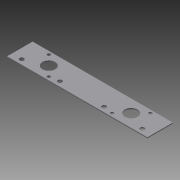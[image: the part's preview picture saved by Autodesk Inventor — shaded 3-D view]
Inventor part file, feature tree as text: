
AUTODESK INVENTOR PART (.ipt)
format: ipt  version: 2013 (Build 170138000, 138)  size: 105,472 bytes
history: native  units: in
note: dims shown in document units (in); Inventor stores cm internally (conversion verified against a paired STEP export)
features: extrude x1, sketch x1
ambient origin geometry x8: Origin, YZ Plane, XZ Plane, XY Plane, X Axis, Y Axis, Z Axis, Center Point
bodies: Solid1 (feature_tree)
feature tree (2):
  extrude  "Extrusion1"  Depth=2.75in
  sketch  "Sketch1"  dims[d0=5.5in d2=2.75in d3=1.0in d4=0.5in d5=0.125in d6=0.125in d7=4.23in d8=0.635in d9=0.125in d10=0.125in d11=1.0in d12=1.0in d13=0.125in d14=0.125in d15=0.5in d16=0.5in d17=0.1695in d18=0.1695in d19=0.1875in d20=0.1875in d21=0.25in d22=0.25in d23=0.04in d24=0.0in]
